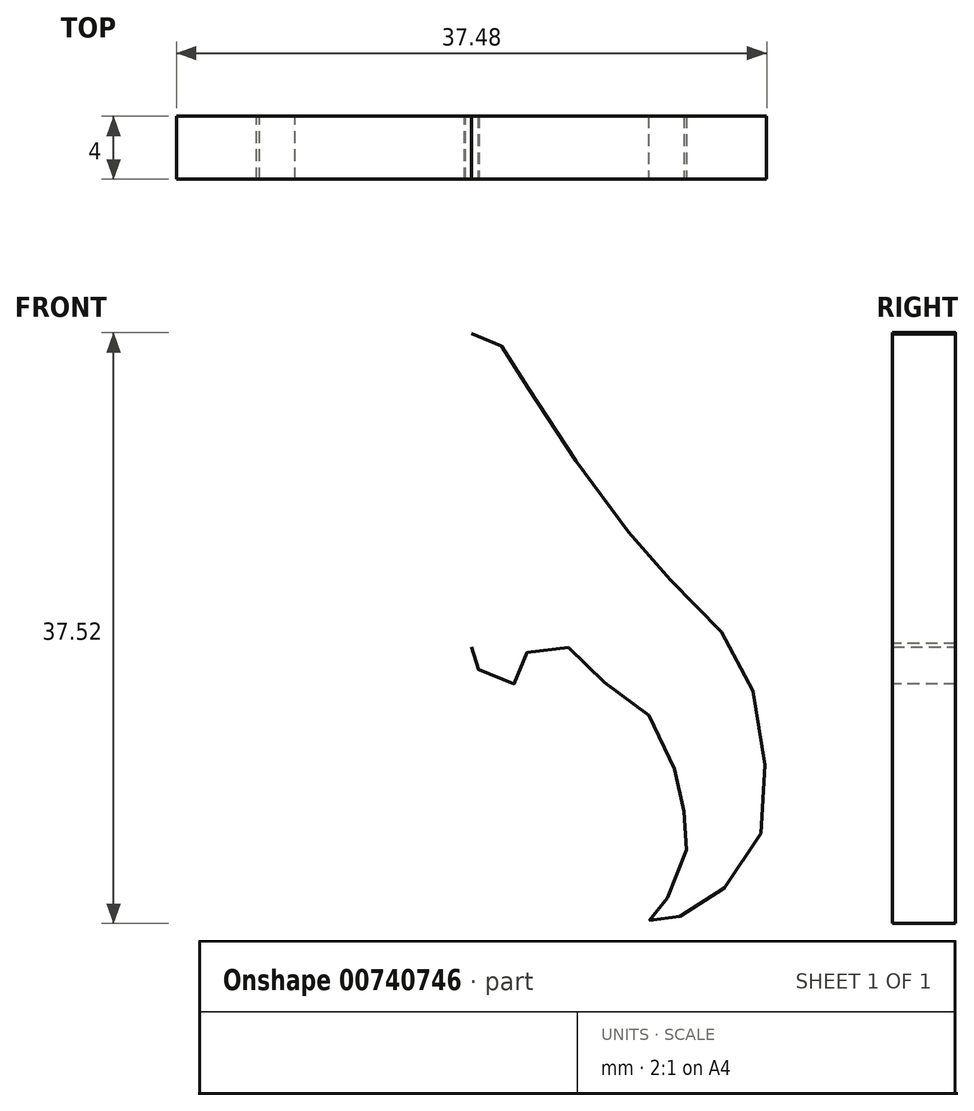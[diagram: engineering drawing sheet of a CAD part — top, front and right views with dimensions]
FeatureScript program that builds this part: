
annotation { "Feature Type Name" : "Feature", "Feature Type Description" : "" }
export const myFeature = defineFeature(function(context is Context, id is Id, definition is map)
    precondition{}
    {
        {
            var Q0;
            Q0=qCreatedBy(makeId("Front.planeOp"),FACE);
            var sketch = newSketch(context, id + "F0", { "sketchPlane" : qUnion([Q0])});
            skFitSpline(sketch, "E0", {"points": [v(0, 18.7) * mm, v(0.28, 18.7) * mm, v(0.87, 18.7) * mm, v(3.3, 16.1) * mm, v(3.7, 14.97) * mm, v(8.73, 7.77) * mm, v(11.16, 4.61) * mm, v(14.7, 0.96) * mm, v(17.3, -2.4) * mm, v(18.5, -7.5) * mm, v(18.58, -12.24) * mm, v(16.66, -15.97) * mm, v(13.9, -17.9) * mm, v(12.63, -18.62) * mm, v(11.62, -18.73) * mm, v(11.22, -18.38) * mm, v(11.76, -17.62) * mm, v(12.71, -16.83) * mm, v(13.65, -14.13) * mm, v(13.5, -13.3) * mm, v(13.45, -11.3) * mm, v(13.1, -9.9) * mm, v(12.18, -6.76) * mm, v(9.93, -4.49) * mm, v(7.8, -2.88) * mm, v(6.1, -1.23) * mm, v(4.15, -1.14) * mm, v(3.19, -2.18) * mm, v(2.93, -3.53) * mm, v(1.58, -3.08) * mm, v(0.45, -2.7) * mm, v(0.43, -1.7) * mm, v(0.13, -1.36) * mm, v(0, -1.21) * mm]});
            skFitSpline(sketch, "E1", {"points": [v(0, 18.7) * mm, v(-0.28, 18.7) * mm, v(-0.87, 18.7) * mm, v(-3.3, 16.1) * mm, v(-3.7, 14.97) * mm, v(-8.73, 7.77) * mm, v(-11.16, 4.61) * mm, v(-14.7, 0.96) * mm, v(-17.3, -2.4) * mm, v(-18.5, -7.5) * mm, v(-18.58, -12.24) * mm, v(-16.66, -15.97) * mm, v(-13.9, -17.9) * mm, v(-12.63, -18.62) * mm, v(-11.62, -18.73) * mm, v(-11.22, -18.38) * mm, v(-11.76, -17.62) * mm, v(-12.71, -16.83) * mm, v(-13.65, -14.13) * mm, v(-13.5, -13.3) * mm, v(-13.45, -11.3) * mm, v(-13.1, -9.9) * mm, v(-12.18, -6.76) * mm, v(-9.93, -4.49) * mm, v(-7.8, -2.88) * mm, v(-6.1, -1.23) * mm, v(-4.15, -1.14) * mm, v(-3.19, -2.18) * mm, v(-2.93, -3.53) * mm, v(-1.58, -3.08) * mm, v(-0.45, -2.7) * mm, v(-0.43, -1.7) * mm, v(-0.13, -1.36) * mm, v(0, -1.21) * mm]});
            skSolve(sketch);
        }
        {
            var Q0;
            Q0=qCreatedBy(makeId("Front.planeOp"),FACE);
            cPlane(context, id + "F1", {"entities" : qUnion([Q0]), "cplaneType" : CPlaneType.OFFSET, "offset" : 4 * mm, "width" : 150 * mm, "height" : 150 * mm});
        }
        {
            var Q0;
            Q0=makeQuery(id+"F0.imprint","IMPRINT",FACE,{"disambiguationData":[TD([[makeQuery(id+"F0.imprint","IMPRINT",EDGE,{"derivedFrom":sQuery(id+"F0.wireOp",EDGE,"E0")}),-1.0]])]});
            var Q1;
            Q1=sQuery(id+"F0.wireOp",EDGE,"E1");
            var Q2;
            Q2=sQuery(id+"F0.wireOp",EDGE,"E0");
            extrude(context, id + "F2", {"entities" : qUnion([Q0]), "surfaceEntities" : qUnion([Q1, Q2]), "depth" : 4 * mm, "offsetDistance" : 25 * mm});
        }
    });
